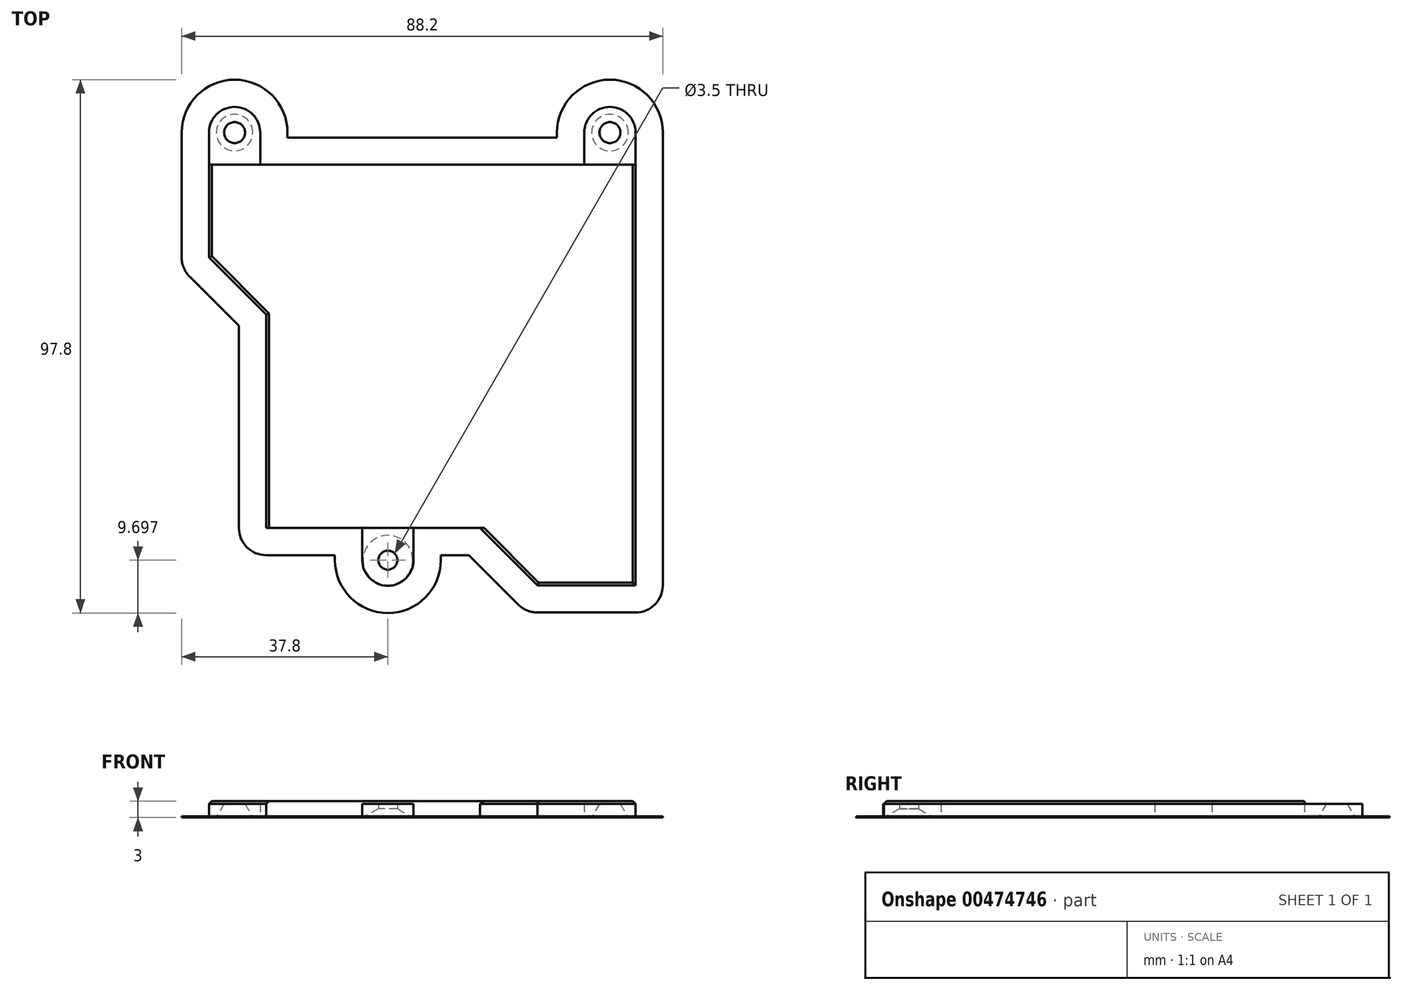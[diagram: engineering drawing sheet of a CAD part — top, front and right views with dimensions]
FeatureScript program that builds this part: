
annotation { "Feature Type Name" : "Feature", "Feature Type Description" : "" }
export const myFeature = defineFeature(function(context is Context, id is Id, definition is map)
    precondition{}
    {
        {
            var Q0;
            Q0=qCreatedBy(makeId("Top.planeOp"),FACE);
            var sketch = newSketch(context, id + "F0", { "sketchPlane" : qUnion([Q0])});
            skLineSegment(sketch, "E0", {"start": v(0, 0) * mm, "end": v(0, -39.5) * mm, "construction": true});
            skLineSegment(sketch, "E1", {"start": v(0, -39.5) * mm, "end": v(17.6, -39.5) * mm, "construction": true});
            skLineSegment(sketch, "E2", {"start": v(39.56, -39.5) * mm, "end": v(50.07, -50) * mm, "construction": true});
            skLineSegment(sketch, "E3", {"start": v(50.07, -50) * mm, "end": v(68.9, -50) * mm, "construction": true});
            skLineSegment(sketch, "E4", {"start": v(68.9, -50) * mm, "end": v(68.9, 33.6) * mm, "construction": true});
            skLineSegment(sketch, "E5", {"start": v(58.3, 28.3) * mm, "end": v(0.1, 28.3) * mm, "construction": true});
            skLineSegment(sketch, "E6", {"start": v(-10.5, 33.6) * mm, "end": v(-10.5, 10.48) * mm, "construction": true});
            skLineSegment(sketch, "E7", {"start": v(-10.5, 10.48) * mm, "end": v(0, 0) * mm, "construction": true});
            skCircle(sketch, "E8", {"center": v(22.9, -44.8) * mm, "radius": 1.4 * mm, "construction": true});
            skCircle(sketch, "E9", {"center": v(-5.2, 33.6) * mm, "radius": 1.4 * mm, "construction": true});
            skCircle(sketch, "E10", {"center": v(63.6, 33.6) * mm, "radius": 1.4 * mm, "construction": true});
            skLineSegment(sketch, "E11", {"start": v(0.1, 28.3) * mm, "end": v(0.1, 33.6) * mm, "construction": true});
            skArc(sketch, "E12", {"start": v(0.1, 33.6) * mm, "mid": v(-5.2, 38.9) * mm, "end": v(-10.5, 33.6) * mm, "construction": true});
            skLineSegment(sketch, "E13", {"start": v(58.3, 28.3) * mm, "end": v(58.3, 33.6) * mm, "construction": true});
            skArc(sketch, "E14", {"start": v(68.9, 33.6) * mm, "mid": v(63.6, 38.9) * mm, "end": v(58.3, 33.6) * mm, "construction": true});
            skLineSegment(sketch, "E15", {"start": v(17.6, -39.5) * mm, "end": v(17.6, -44.8) * mm, "construction": true});
            skLineSegment(sketch, "E16", {"start": v(28.2, -39.5) * mm, "end": v(28.2, -44.8) * mm, "construction": true});
            skArc(sketch, "E17", {"start": v(17.6, -44.8) * mm, "mid": v(22.9, -50.1) * mm, "end": v(28.2, -44.8) * mm, "construction": true});
            skLineSegment(sketch, "E18.trimOffspring", {"start": v(28.2, -39.5) * mm, "end": v(39.56, -39.5) * mm, "construction": true});
            skCircle(sketch, "E19", {"center": v(22.9, -44.8) * mm, "radius": 1.75 * mm});
            skCircle(sketch, "E20", {"center": v(-5.2, 33.6) * mm, "radius": 1.75 * mm});
            skCircle(sketch, "E21", {"center": v(63.6, 33.6) * mm, "radius": 1.75 * mm});
            skLineSegment(sketch, "E22", {"start": v(18.2, -44.8) * mm, "end": v(18.2, -38.9) * mm});
            skLineSegment(sketch, "E23", {"start": v(18.2, -38.9) * mm, "end": v(0.6, -38.9) * mm});
            skLineSegment(sketch, "E24", {"start": v(27.6, -44.8) * mm, "end": v(27.6, -38.9) * mm});
            skArc(sketch, "E25", {"start": v(18.2, -44.8) * mm, "mid": v(22.9, -49.5) * mm, "end": v(27.6, -44.8) * mm});
            skLineSegment(sketch, "E26", {"start": v(0.6, -38.9) * mm, "end": v(0.6, 0.25) * mm});
            skLineSegment(sketch, "E27", {"start": v(0.6, 0.25) * mm, "end": v(-9.9, 10.73) * mm});
            skLineSegment(sketch, "E28", {"start": v(-9.9, 10.73) * mm, "end": v(-9.9, 33.6) * mm});
            skArc(sketch, "E29", {"start": v(-0.5, 33.6) * mm, "mid": v(-5.2, 38.3) * mm, "end": v(-9.9, 33.6) * mm});
            skLineSegment(sketch, "E30", {"start": v(-0.5, 33.6) * mm, "end": v(-0.5, 27.7) * mm});
            skLineSegment(sketch, "E31", {"start": v(-0.5, 27.7) * mm, "end": v(58.9, 27.7) * mm});
            skLineSegment(sketch, "E32", {"start": v(27.6, -38.9) * mm, "end": v(39.8, -38.9) * mm});
            skLineSegment(sketch, "E33", {"start": v(39.8, -38.9) * mm, "end": v(50.32, -49.4) * mm});
            skLineSegment(sketch, "E34", {"start": v(50.32, -49.4) * mm, "end": v(68.3, -49.4) * mm});
            skLineSegment(sketch, "E35", {"start": v(68.3, -49.4) * mm, "end": v(68.3, 33.6) * mm});
            skArc(sketch, "E36", {"start": v(68.3, 33.6) * mm, "mid": v(63.6, 38.3) * mm, "end": v(58.9, 33.6) * mm});
            skLineSegment(sketch, "E37", {"start": v(58.9, 33.6) * mm, "end": v(58.9, 27.7) * mm});
            skSolve(sketch);
        }
        {
            var Q0;
            Q0=qSketchRegion(id+"F0",true);
            extrude(context, id + "F1", {"entities" : qUnion([Q0]), "depth" : 3 * mm, "offsetDistance" : 25 * mm});
        }
        {
            var Q0;
            Q0=makeQuery(id+"F1.opExtrude","CAP_EDGE",EDGE,{"disambiguationData":[OSD([sQuery(id+"F0.wireOp",EDGE,"E19")])],"isStart":true});
            var Q1;
            Q1=makeQuery(id+"F1.opExtrude","CAP_EDGE",EDGE,{"disambiguationData":[OSD([sQuery(id+"F0.wireOp",EDGE,"E20")])],"isStart":true});
            var Q2;
            Q2=makeQuery(id+"F1.opExtrude","CAP_EDGE",EDGE,{"disambiguationData":[OSD([sQuery(id+"F0.wireOp",EDGE,"E21")])],"isStart":true});
            chamfer(context, id + "F2", {"entities" : qUnion([Q0, Q1, Q2]), "chamferType" : ChamferType.TWO_OFFSETS, "width1" : 1.6 * mm, "oppositeDirection" : false, "width2" : 2.8 * mm, "tangentPropagation" : true});
        }
        {
            var Q0;
            Q0=makeQuery(id+"F1.opExtrude","CAP_FACE",FACE,{"disambiguationData":[OSD([sQuery(id+"F0.wireOp",EDGE,"E19"),sQuery(id+"F0.wireOp",EDGE,"E20"),sQuery(id+"F0.wireOp",EDGE,"E21"),sQuery(id+"F0.wireOp",EDGE,"E22"),sQuery(id+"F0.wireOp",EDGE,"E23"),sQuery(id+"F0.wireOp",EDGE,"E24"),sQuery(id+"F0.wireOp",EDGE,"E25"),sQuery(id+"F0.wireOp",EDGE,"E26"),sQuery(id+"F0.wireOp",EDGE,"E27"),sQuery(id+"F0.wireOp",EDGE,"E28"),sQuery(id+"F0.wireOp",EDGE,"E29"),sQuery(id+"F0.wireOp",EDGE,"E30"),sQuery(id+"F0.wireOp",EDGE,"E31"),sQuery(id+"F0.wireOp",EDGE,"E32"),sQuery(id+"F0.wireOp",EDGE,"E33"),sQuery(id+"F0.wireOp",EDGE,"E34"),sQuery(id+"F0.wireOp",EDGE,"E35"),sQuery(id+"F0.wireOp",EDGE,"E36"),sQuery(id+"F0.wireOp",EDGE,"E37")])],"isStart":false});
            var sketch = newSketch(context, id + "F3", { "sketchPlane" : qUnion([Q0])});
            skLineSegment(sketch, "E38", {"start": v(-0.5, 27.7) * mm, "end": v(-9.9, 27.7) * mm});
            skLineSegment(sketch, "E39", {"start": v(-9.9, 27.7) * mm, "end": v(-9.9, 33.6) * mm});
            skArc(sketch, "E40", {"start": v(-0.5, 33.6) * mm, "mid": v(-5.2, 38.3) * mm, "end": v(-9.9, 33.6) * mm});
            skLineSegment(sketch, "E41", {"start": v(-0.5, 33.6) * mm, "end": v(-0.5, 27.7) * mm});
            skLineSegment(sketch, "E42", {"start": v(58.9, 27.7) * mm, "end": v(68.3, 27.7) * mm});
            skLineSegment(sketch, "E43", {"start": v(68.3, 27.7) * mm, "end": v(68.3, 33.6) * mm});
            skArc(sketch, "E44", {"start": v(68.3, 33.6) * mm, "mid": v(63.6, 38.3) * mm, "end": v(58.9, 33.6) * mm});
            skLineSegment(sketch, "E45", {"start": v(58.9, 33.6) * mm, "end": v(58.9, 27.7) * mm});
            skLineSegment(sketch, "E46", {"start": v(18.2, -38.9) * mm, "end": v(27.6, -38.9) * mm});
            skLineSegment(sketch, "E47", {"start": v(27.6, -38.9) * mm, "end": v(27.6, -44.8) * mm});
            skArc(sketch, "E48", {"start": v(18.2, -44.8) * mm, "mid": v(22.9, -49.5) * mm, "end": v(27.6, -44.8) * mm});
            skLineSegment(sketch, "E49", {"start": v(18.2, -38.9) * mm, "end": v(18.2, -44.8) * mm});
            skSolve(sketch);
        }
        {
            var Q0;
            Q0 = qSketchRegion(id + "F3", true);
            extrude(context, id + "F4", {"entities" : qUnion([Q0]), "operationType" : NewBodyOperationType.REMOVE, "oppositeDirection" : true, "depth" : 0.5 * mm, "offsetDistance" : 25 * mm});
        }
        {
            var Q0;
            Q0=makeQuery(id+"F4.boolean.opBoolean","MERGE",EDGE,{"derivedFrom":[makeQuery(id+"F1.opExtrude","CAP_EDGE",EDGE,{"disambiguationData":[OSD([sQuery(id+"F0.wireOp",EDGE,"E31")])],"isStart":false})],"fromTools":[makeQuery(id+"F4.opExtrude","CAP_EDGE",EDGE,{"disambiguationData":[OSD([sQuery(id+"F3.wireOp",EDGE,"E38")])],"isStart":true}),makeQuery(id+"F4.opExtrude","CAP_EDGE",EDGE,{"disambiguationData":[OSD([sQuery(id+"F3.wireOp",EDGE,"E42")])],"isStart":true})]});
            var Q1;
            Q1=makeQuery(id+"F1.opExtrude","CAP_EDGE",EDGE,{"disambiguationData":[OSD([sQuery(id+"F0.wireOp",EDGE,"E28")])],"isStart":false});
            var Q2;
            Q2=makeQuery(id+"F1.opExtrude","CAP_EDGE",EDGE,{"disambiguationData":[OSD([sQuery(id+"F0.wireOp",EDGE,"E27")])],"isStart":false});
            var Q3;
            Q3=makeQuery(id+"F1.opExtrude","CAP_EDGE",EDGE,{"disambiguationData":[OSD([sQuery(id+"F0.wireOp",EDGE,"E26")])],"isStart":false});
            var Q4;
            Q4=makeQuery(id+"F4.boolean.opBoolean","MERGE",EDGE,{"derivedFrom":[makeQuery(id+"F1.opExtrude","CAP_EDGE",EDGE,{"disambiguationData":[OSD([sQuery(id+"F0.wireOp",EDGE,"E23")])],"isStart":false}),makeQuery(id+"F1.opExtrude","CAP_EDGE",EDGE,{"disambiguationData":[OSD([sQuery(id+"F0.wireOp",EDGE,"E32")])],"isStart":false})],"fromTools":[makeQuery(id+"F4.opExtrude","CAP_EDGE",EDGE,{"disambiguationData":[OSD([sQuery(id+"F3.wireOp",EDGE,"E46")])],"isStart":true})]});
            var Q5;
            Q5=makeQuery(id+"F1.opExtrude","CAP_EDGE",EDGE,{"disambiguationData":[OSD([sQuery(id+"F0.wireOp",EDGE,"E33")])],"isStart":false});
            var Q6;
            Q6=makeQuery(id+"F1.opExtrude","CAP_EDGE",EDGE,{"disambiguationData":[OSD([sQuery(id+"F0.wireOp",EDGE,"E34")])],"isStart":false});
            var Q7;
            Q7=makeQuery(id+"F1.opExtrude","CAP_EDGE",EDGE,{"disambiguationData":[OSD([sQuery(id+"F0.wireOp",EDGE,"E35")])],"isStart":false});
            chamfer(context, id + "F5", {"entities" : qUnion([Q0, Q1, Q2, Q3, Q4, Q5, Q6, Q7]), "width" : 0.5 * mm, "tangentPropagation" : true});
        }
        {
            var Q0;
            Q0=makeQuery(id+"F1.opExtrude","CAP_FACE",FACE,{"disambiguationData":[OSD([sQuery(id+"F0.wireOp",EDGE,"E19"),sQuery(id+"F0.wireOp",EDGE,"E20"),sQuery(id+"F0.wireOp",EDGE,"E21"),sQuery(id+"F0.wireOp",EDGE,"E22"),sQuery(id+"F0.wireOp",EDGE,"E23"),sQuery(id+"F0.wireOp",EDGE,"E24"),sQuery(id+"F0.wireOp",EDGE,"E25"),sQuery(id+"F0.wireOp",EDGE,"E26"),sQuery(id+"F0.wireOp",EDGE,"E27"),sQuery(id+"F0.wireOp",EDGE,"E28"),sQuery(id+"F0.wireOp",EDGE,"E29"),sQuery(id+"F0.wireOp",EDGE,"E30"),sQuery(id+"F0.wireOp",EDGE,"E31"),sQuery(id+"F0.wireOp",EDGE,"E32"),sQuery(id+"F0.wireOp",EDGE,"E33"),sQuery(id+"F0.wireOp",EDGE,"E34"),sQuery(id+"F0.wireOp",EDGE,"E35"),sQuery(id+"F0.wireOp",EDGE,"E36"),sQuery(id+"F0.wireOp",EDGE,"E37")])],"isStart":true});
            var sketch = newSketch(context, id + "F6", { "sketchPlane" : qUnion([Q0])});
            skLineSegment(sketch, "E50", {"start": v(-9.9, -10.73) * mm, "end": v(0.6, -0.25) * mm});
            skLineSegment(sketch, "E51", {"start": v(0.6, -0.25) * mm, "end": v(0.6, 38.9) * mm});
            skLineSegment(sketch, "E52", {"start": v(0.6, 38.9) * mm, "end": v(18.2, 38.9) * mm});
            skLineSegment(sketch, "E53", {"start": v(18.2, 38.9) * mm, "end": v(18.2, 44.8) * mm});
            skLineSegment(sketch, "E54", {"start": v(27.6, 44.8) * mm, "end": v(27.6, 38.9) * mm});
            skLineSegment(sketch, "E55", {"start": v(27.6, 38.9) * mm, "end": v(39.8, 38.9) * mm});
            skLineSegment(sketch, "E56", {"start": v(39.8, 38.9) * mm, "end": v(50.32, 49.4) * mm});
            skLineSegment(sketch, "E57", {"start": v(50.32, 49.4) * mm, "end": v(68.3, 49.4) * mm});
            skLineSegment(sketch, "E58", {"start": v(68.3, 49.4) * mm, "end": v(68.3, -33.6) * mm});
            skLineSegment(sketch, "E59", {"start": v(-9.9, -10.73) * mm, "end": v(-9.9, -33.6) * mm});
            skLineSegment(sketch, "E60", {"start": v(-0.5, -33.6) * mm, "end": v(-0.5, -27.7) * mm});
            skLineSegment(sketch, "E61", {"start": v(-0.5, -27.7) * mm, "end": v(58.9, -27.7) * mm});
            skLineSegment(sketch, "E62", {"start": v(58.9, -27.7) * mm, "end": v(58.9, -33.6) * mm});
            skArc(sketch, "E63", {"start": v(-9.9, -33.6) * mm, "mid": v(-5.2, -38.3) * mm, "end": v(-0.5, -33.6) * mm});
            skArc(sketch, "E64", {"start": v(58.9, -33.6) * mm, "mid": v(63.6, -38.3) * mm, "end": v(68.3, -33.6) * mm});
            skArc(sketch, "E65", {"start": v(27.6, 44.8) * mm, "mid": v(22.9, 49.5) * mm, "end": v(18.2, 44.8) * mm});
            skLineSegment(sketch, "E66", {"start": v(-4.4, 38.9) * mm, "end": v(-4.4, 1.82) * mm});
            skLineSegment(sketch, "E67", {"start": v(-4.4, 1.82) * mm, "end": v(-13.43, -7.2) * mm});
            skLineSegment(sketch, "E68", {"start": v(0.6, 43.9) * mm, "end": v(13.2, 43.9) * mm});
            skArc(sketch, "E69", {"start": v(0.6, 43.9) * mm, "mid": v(-2.94, 42.43) * mm, "end": v(-4.4, 38.9) * mm});
            skArc(sketch, "E70", {"start": v(32.6, 44.8) * mm, "mid": v(22.9, 54.5) * mm, "end": v(13.2, 44.8) * mm});
            skLineSegment(sketch, "E71", {"start": v(13.2, 44.8) * mm, "end": v(13.2, 43.9) * mm});
            skLineSegment(sketch, "E72", {"start": v(-14.9, -10.73) * mm, "end": v(-14.9, -33.6) * mm});
            skArc(sketch, "E73", {"start": v(-13.43, -7.2) * mm, "mid": v(-14.52, -8.81) * mm, "end": v(-14.9, -10.73) * mm});
            skArc(sketch, "E74", {"start": v(-14.9, -33.6) * mm, "mid": v(-5.2, -43.3) * mm, "end": v(4.5, -33.6) * mm});
            skLineSegment(sketch, "E75", {"start": v(4.5, -33.6) * mm, "end": v(4.5, -32.7) * mm});
            skLineSegment(sketch, "E76", {"start": v(4.5, -32.7) * mm, "end": v(53.9, -32.7) * mm});
            skLineSegment(sketch, "E77", {"start": v(53.9, -32.7) * mm, "end": v(53.9, -33.6) * mm});
            skArc(sketch, "E78", {"start": v(53.9, -33.6) * mm, "mid": v(63.6, -43.3) * mm, "end": v(73.3, -33.6) * mm});
            skLineSegment(sketch, "E79", {"start": v(73.3, -33.6) * mm, "end": v(73.3, 49.4) * mm});
            skArc(sketch, "E80", {"start": v(73.3, 49.4) * mm, "mid": v(71.84, 52.93) * mm, "end": v(68.3, 54.4) * mm});
            skLineSegment(sketch, "E81", {"start": v(68.3, 54.4) * mm, "end": v(50.32, 54.4) * mm});
            skArc(sketch, "E82", {"start": v(50.32, 54.4) * mm, "mid": v(48.41, 54.01) * mm, "end": v(46.79, 52.93) * mm});
            skLineSegment(sketch, "E83", {"start": v(46.79, 52.93) * mm, "end": v(37.74, 43.9) * mm});
            skLineSegment(sketch, "E84", {"start": v(32.6, 44.8) * mm, "end": v(32.6, 43.9) * mm});
            skLineSegment(sketch, "E85", {"start": v(32.6, 43.9) * mm, "end": v(37.74, 43.9) * mm});
            skSolve(sketch);
        }
        {
            var Q0;
            Q0 = qSketchRegion(id + "F6", true);
            extrude(context, id + "F7", {"entities" : qUnion([Q0]), "operationType" : NewBodyOperationType.ADD, "oppositeDirection" : true, "depth" : 0.2 * mm, "offsetDistance" : 25 * mm});
        }
    });
